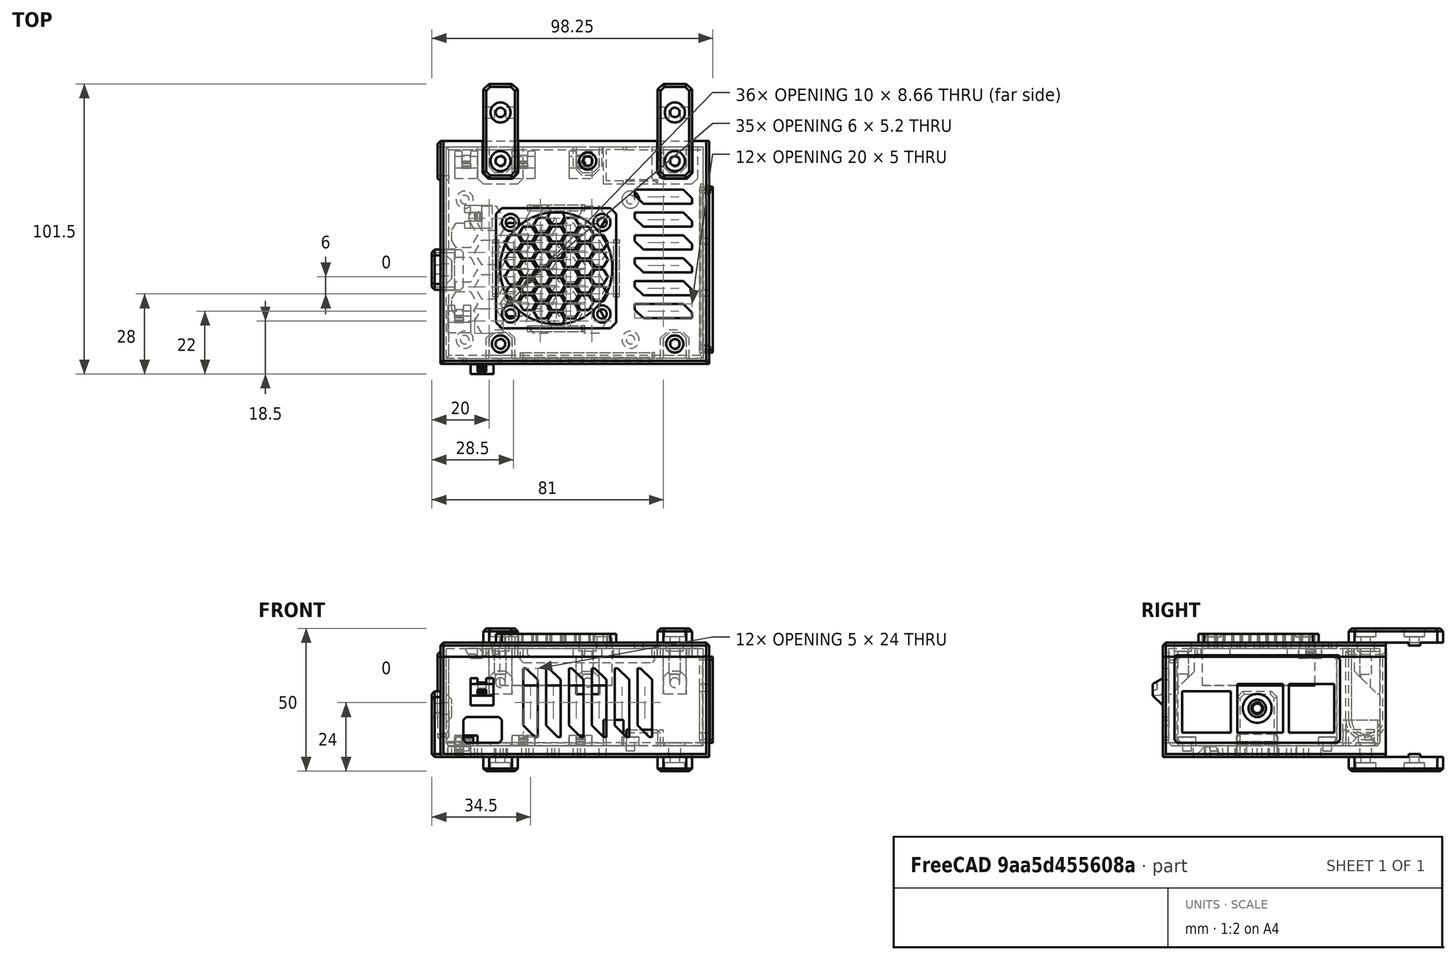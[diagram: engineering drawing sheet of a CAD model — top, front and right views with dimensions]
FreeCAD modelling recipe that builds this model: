
FCSTD DOCUMENT  (FreeCAD 0.18R16146 (Git))
Label: pi-mounter
License: All rights reserved
LicenseURL: http://en.wikipedia.org/wiki/All_rights_reserved
objects: Part::Cylinder×54, Part::MultiFuse×53, Part::Feature×52, Part::Box×50, Part::Chamfer×30, Part::Cut×28, Mesh::Feature×2
note: 267 computed .brp shape members not serialized (recipe doc carries the construction recipe); baked Part::Feature solids carry a one-line shape summary decoded from their .brp

FEATURE [Mesh::Feature] pi_pref  label="pi-pref001"
  Placement = pos=(3.5,-6,7.5) rot=(0,0,1;0rad)
FEATURE [Part::Feature] Cut003002006013012002001001_solid  label="io-panel"
  shape: bbox 4.5 x 58 x 30 mm, 38 faces (baked)
FEATURE [Part::Feature] Common001_solid  label="Common001 (Solid)"
  shape: bbox 92 x 61 x 35 mm, 183 faces (baked)
FEATURE [Part::Feature] Cut003002006013012006010  label="case-bolt012"
  Placement = pos=(19,60,25) rot=(0,0,-1;1.5708rad)
  shape: bbox 8 x 9 x 13 mm, 12 faces (baked)
FEATURE [Part::Feature] Part__Feature003  label="zip-tie-slot002"
  Placement = pos=(22.5,54,4) rot=(0,0,1;0rad)
  shape: bbox 8 x 9.5 x 3.5 mm, 30 faces (baked)
FEATURE [Part::Feature] Part__Feature005  label="zip-tie-slot004"
  Placement = pos=(2.5,54,4) rot=(0,0,1;0rad)
  shape: bbox 8 x 9.5 x 3.5 mm, 30 faces (baked)
FEATURE [Part::Cylinder] Cylinder
  Angle = 360
  AttacherType = Attacher::AttachEngine3D
  Height = 3.2
  Placement = pos=(6.5,-2.5,0) rot=(0,0,1;0rad)
  Radius = 4
FEATURE [Part::Cylinder] Cylinder001
  Angle = 360
  AttacherType = Attacher::AttachEngine3D
  Height = 3.2
  Placement = pos=(6.5,46.5,0) rot=(0,0,1;0rad)
  Radius = 4
FEATURE [Part::Cylinder] Cylinder002
  Angle = 360
  AttacherType = Attacher::AttachEngine3D
  Height = 3.2
  Placement = pos=(64.5,46.5,0) rot=(0,0,1;0rad)
  Radius = 4
FEATURE [Part::Cylinder] Cylinder003
  Angle = 360
  AttacherType = Attacher::AttachEngine3D
  Height = 3.2
  Placement = pos=(64.5,-2.5,0) rot=(0,0,1;0rad)
  Radius = 4
FEATURE [Part::Cylinder] Cylinder004
  Angle = 360
  AttacherType = Attacher::AttachEngine3D
  Height = 4
  Placement = pos=(60,20.75,0) rot=(0,0,1;0rad)
  Radius = 4
FEATURE [Part::MultiFuse] Fusion
  Shapes = -> [Cylinder004,Common001_solid]
FEATURE [Part::Cylinder] Cylinder005
  Angle = 360
  AttacherType = Attacher::AttachEngine3D
  Height = 7.5
  Placement = pos=(64.5,-2.5,0) rot=(0,0,1;0rad)
  Radius = 1.5
FEATURE [Part::Cylinder] Cylinder006
  Angle = 360
  AttacherType = Attacher::AttachEngine3D
  Height = 7.5
  Placement = pos=(64.5,46.5,0) rot=(0,0,1;0rad)
  Radius = 1.5
FEATURE [Part::Cylinder] Cylinder007
  Angle = 360
  AttacherType = Attacher::AttachEngine3D
  Height = 7.5
  Placement = pos=(6.5,-2.5,0) rot=(0,0,1;0rad)
  Radius = 1.5
FEATURE [Part::Cylinder] Cylinder008
  Angle = 360
  AttacherType = Attacher::AttachEngine3D
  Height = 7.5
  Placement = pos=(6.5,46.5,0) rot=(0,0,1;0rad)
  Radius = 1.5
FEATURE [Part::MultiFuse] Fusion001
  Shapes = -> [Cylinder003,Cylinder002,Cylinder,Cylinder001]
FEATURE [Part::MultiFuse] Fusion002
  Shapes = -> [Fusion,Fusion001]
FEATURE [Part::Cylinder] Cylinder009
  Angle = 360
  AttacherType = Attacher::AttachEngine3D
  Height = 2
  Placement = pos=(64.5,-2.5,0) rot=(0,0,1;0rad)
  Radius = 2
FEATURE [Part::Cylinder] Cylinder010
  Angle = 360
  AttacherType = Attacher::AttachEngine3D
  Height = 2
  Placement = pos=(64.5,46.5,0) rot=(0,0,1;0rad)
  Radius = 2
FEATURE [Part::Cylinder] Cylinder011
  Angle = 360
  AttacherType = Attacher::AttachEngine3D
  Height = 2
  Placement = pos=(6.5,-2.5,0) rot=(0,0,1;0rad)
  Radius = 2
FEATURE [Part::Cylinder] Cylinder012
  Angle = 360
  AttacherType = Attacher::AttachEngine3D
  Height = 2
  Placement = pos=(6.5,46.5,0) rot=(0,0,1;0rad)
  Radius = 2
FEATURE [Part::MultiFuse] Fusion003
  Shapes = -> [Cylinder005,Cylinder006,Cylinder007,Cylinder008]
FEATURE [Part::Cut] Cut
  Base = -> Fusion002
  Tool = -> Fusion003
FEATURE [Part::MultiFuse] Fusion004
  Shapes = -> [Cylinder012,Cylinder009,Cylinder010,Cylinder011]
FEATURE [Part::MultiFuse] Fusion005
  Shapes = -> [Cut,Fusion004]
FEATURE [Part::Box] Box  label="Cube"
  AttacherType = Attacher::AttachEngine3D
  Height = 10
  Length = 2
  Placement = pos=(18,-2,5.5) rot=(0,0,1;0rad)
  Width = 3
FEATURE [Part::Box] Box001  label="Cube001"
  AttacherType = Attacher::AttachEngine3D
  Height = 10
  Length = 21
  Placement = pos=(-1,-1,0) rot=(0,0,1;0rad)
  Width = 13
FEATURE [Part::Box] Box002  label="Cube002"
  AttacherType = Attacher::AttachEngine3D
  Height = 10
  Length = 19
  Placement = pos=(0,0,1) rot=(0,0,1;0rad)
  Width = 11
FEATURE [Part::Cut] Cut003002006013012006011
  Base = -> Box001
  Tool = -> Box002
FEATURE [Part::Box] Box003  label="Cube003"
  AttacherType = Attacher::AttachEngine3D
  Height = 10
  Length = 1
  Placement = pos=(6,-2,1) rot=(0,0,1;0rad)
  Width = 15
FEATURE [Part::Box] Box004  label="Cube004"
  AttacherType = Attacher::AttachEngine3D
  Height = 10
  Length = 2
  Placement = pos=(18,10,5.5) rot=(0,0,1;0rad)
  Width = 3
FEATURE [Part::MultiFuse] Fusion006
  Placement = pos=(0,0,-4.5) rot=(0,0,1;0rad)
  Shapes = -> [Box004,Box]
FEATURE [Part::Cut] Cut003002006013012006012
  Base = -> Cut003002006013012006011
  Tool = -> Box003
FEATURE [Part::Cut] Cut003002006013012006013
  Base = -> Cut003002006013012006012
  Tool = -> Fusion006
FEATURE [Part::Cylinder] Cylinder013
  Angle = 360
  AttacherType = Attacher::AttachEngine3D
  Height = 11
  Placement = pos=(7,0,6) rot=(0,1,0;1.5708rad)
  Radius = 0.5
FEATURE [Part::Cylinder] Cylinder014
  Angle = 360
  AttacherType = Attacher::AttachEngine3D
  Height = 11
  Placement = pos=(7,11,6) rot=(0,1,0;1.5708rad)
  Radius = 0.5
FEATURE [Part::Cylinder] Cylinder015
  Angle = 360
  AttacherType = Attacher::AttachEngine3D
  Height = 9
  Placement = pos=(19,10,6) rot=(0.57735,0.57735,-0.57735;2.0944rad)
  Radius = 0.5
FEATURE [Part::MultiFuse] Fusion007
  Shapes = -> [Cylinder015,Cylinder014,Cylinder013,Cut003002006013012006013]
FEATURE [Part::Box] Box005  label="Cube005"
  AttacherType = Attacher::AttachEngine3D
  Height = 10
  Length = 15
  Placement = pos=(7,-2,6.5) rot=(0,0,1;0rad)
  Width = 15
FEATURE [Part::Cut] Cut003002006013012006014  label="dcdc-mounter"
  Base = -> Fusion007
  Placement = pos=(56,53,3) rot=(0,0,1;0rad)
  Tool = -> Box005
FEATURE [Part::Feature] Part__Feature006  label="zip-tie-slot005"
  Placement = pos=(42.5,54,4) rot=(0,0,1;0rad)
  shape: bbox 8 x 9.5 x 3.5 mm, 30 faces (baked)
FEATURE [Part::Box] Box006  label="Cube006"
  AttacherType = Attacher::AttachEngine3D
  Height = 4
  Length = 92
  Placement = pos=(0,52,0) rot=(0,0,1;0rad)
  Width = 13
FEATURE [Part::Box] Box007  label="Cube007"
  AttacherType = Attacher::AttachEngine3D
  Height = 35
  Length = 92
  Placement = pos=(0,-11,0) rot=(0,0,1;0rad)
  Width = 2
FEATURE [Part::Box] Box008  label="Cube008"
  AttacherType = Attacher::AttachEngine3D
  Height = 35
  Length = 92
  Placement = pos=(0,65,0) rot=(0,0,1;0rad)
  Width = 2
FEATURE [Part::Box] Box009  label="Cube009"
  AttacherType = Attacher::AttachEngine3D
  Height = 35
  Length = 2
  Placement = pos=(90,52,0) rot=(0,0,1;0rad)
  Width = 13
FEATURE [Part::Box] Box010  label="Cube010"
  AttacherType = Attacher::AttachEngine3D
  Height = 35
  Length = 2
  Placement = pos=(-2,-11,0) rot=(0,0,1;0rad)
  Width = 78
FEATURE [Part::Box] Box011  label="Cube011"
  AttacherType = Attacher::AttachEngine3D
  Height = 4
  Length = 92
  Placement = pos=(0,-11,0) rot=(0,0,1;0rad)
  Width = 4
FEATURE [Part::Box] Box012  label="Cube012"
  AttacherType = Attacher::AttachEngine3D
  Height = 4
  Length = 4
  Placement = pos=(-2,-11,0) rot=(0,0,1;0rad)
  Width = 78
FEATURE [Part::MultiFuse] Fusion008
  Shapes = -> [Box012,Box010]
FEATURE [Part::MultiFuse] Fusion009
  Shapes = -> [Box006,Box008]
FEATURE [Part::MultiFuse] Fusion010
  Shapes = -> [Box011,Box007]
FEATURE [Part::Chamfer] Chamfer
  Base = -> Fusion008
  Edges = 1 edges r=1: [Edge28]
FEATURE [Part::Chamfer] Chamfer001
  Base = -> Fusion009
  Edges = 1 edges r=1: [Edge8]
FEATURE [Part::Chamfer] Chamfer002
  Base = -> Fusion010
  Edges = 1 edges r=1: [Edge23]
FEATURE [Part::MultiFuse] Fusion011
  Shapes = -> [Chamfer002,Chamfer001,Chamfer,Fusion005]
FEATURE [Part::MultiFuse] Fusion012
  Shapes = -> [Fusion011,Part__Feature006,Part__Feature003,Part__Feature005]
FEATURE [Part::Cylinder] Cylinder016
  Angle = 360
  AttacherType = Attacher::AttachEngine3D
  Height = 5
  Placement = pos=(19,60,0) rot=(0,0,1;0rad)
  Radius = 3.5
FEATURE [Part::Feature] Cut003002006013012006015  label="case-bolt013"
  Placement = pos=(80,60,25) rot=(0,0,-1;1.5708rad)
  shape: bbox 8 x 9 x 13 mm, 12 faces (baked)
FEATURE [Part::Feature] Cut003002006013012006016  label="case-bolt014"
  Placement = pos=(49.5,60,25) rot=(0,0,-1;1.5708rad)
  shape: bbox 8 x 9 x 13 mm, 12 faces (baked)
FEATURE [Part::Cylinder] Cylinder017
  Angle = 360
  AttacherType = Attacher::AttachEngine3D
  Height = 5
  Placement = pos=(80,60,0) rot=(0,0,1;0rad)
  Radius = 3.5
FEATURE [Part::Cylinder] Cylinder018
  Angle = 360
  AttacherType = Attacher::AttachEngine3D
  Height = 5
  Placement = pos=(80,60,0) rot=(0,0,1;0rad)
  Radius = 2.05
FEATURE [Part::Cylinder] Cylinder019
  Angle = 360
  AttacherType = Attacher::AttachEngine3D
  Height = 5
  Placement = pos=(19,60,0) rot=(0,0,1;0rad)
  Radius = 2.05
FEATURE [Part::MultiFuse] Fusion013
  Shapes = -> [Cylinder017,Cylinder016]
FEATURE [Part::MultiFuse] Fusion014
  Shapes = -> [Cylinder019,Cylinder018]
FEATURE [Part::MultiFuse] Fusion015
  Shapes = -> [Fusion012,Fusion013]
FEATURE [Part::Cut] Cut003002006013012006017
  Base = -> Fusion015
  Tool = -> Fusion014
FEATURE [Part::Feature] Cut003002006013012006018  label="case-bolt015"
  Placement = pos=(19,-4,25) rot=(0,0,1;1.5708rad)
  shape: bbox 8 x 9 x 13 mm, 12 faces (baked)
FEATURE [Part::Feature] Cut003002006013012006019  label="case-bolt016"
  Placement = pos=(80,-4,25) rot=(0,0,1;1.5708rad)
  shape: bbox 8 x 9 x 13 mm, 12 faces (baked)
FEATURE [Part::MultiFuse] Fusion016
  Shapes = -> [Cut003002006013012006019,Cut003002006013012006018,Cut003002006013012006017,Cut003002006013012006016,Cut003002006013012006015,Box009,Cut003002006013012006014,Cut003002006013012006010]
FEATURE [Part::Cylinder] Cylinder020
  Angle = 360
  AttacherType = Attacher::AttachEngine3D
  Height = 10
  Placement = pos=(-7,60,13) rot=(0,1,0;1.5708rad)
  Radius = 5
FEATURE [Part::Cylinder] Cylinder021
  Angle = 360
  AttacherType = Attacher::AttachEngine3D
  Height = 4
  Placement = pos=(-3,60,13) rot=(0,1,0;1.5708rad)
  Radius = 7
FEATURE [Part::Chamfer] Chamfer003
  Base = -> Cylinder021
  Edges = 2 edges r=1: [Edge1,Edge3]
FEATURE [Part::MultiFuse] Fusion017
  Shapes = -> [Fusion016,Chamfer003]
FEATURE [Part::Box] Box013  label="Cube013"
  AttacherType = Attacher::AttachEngine3D
  Height = 22
  Length = 10
  Placement = pos=(-7,55,13) rot=(0,0,1;0rad)
  Width = 10
FEATURE [Part::Box] Box014  label="Cube014"
  AttacherType = Attacher::AttachEngine3D
  Height = 22
  Length = 4
  Placement = pos=(-3,53,13) rot=(0,0,1;0rad)
  Width = 14
FEATURE [Part::Chamfer] Chamfer004
  Base = -> Box014
  Edges = 3 edges r=1: [Edge1,Edge3,Edge5]
FEATURE [Part::MultiFuse] Fusion018
  Shapes = -> [Box013,Cylinder020]
FEATURE [Part::MultiFuse] Fusion019
  Shapes = -> [Fusion017,Chamfer004]
FEATURE [Part::Cut] Cut003002006013012006020
  Base = -> Fusion019
  Tool = -> Fusion018
FEATURE [Part::Box] Box015  label="Cube015"
  AttacherType = Attacher::AttachEngine3D
  Height = 10
  Length = 11
  Placement = pos=(63,54,4) rot=(0,0,1;0rad)
  Width = 10
FEATURE [Part::Cut] Cut003002006013012006021
  Base = -> Cut003002006013012006020
  Tool = -> Box015
FEATURE [Part::Box] Box016  label="Cube016"
  AttacherType = Attacher::AttachEngine3D
  Height = 7
  Length = 13.5
  Placement = pos=(6,-17,7) rot=(0,0,1;0rad)
  Width = 10
FEATURE [Part::Cut] Cut003002006013012006022
  Base = -> Cut003002006013012006021
  Tool = -> Box016
FEATURE [Part::Chamfer] Chamfer005
  Base = -> Cut003002006013012006022
  Edges = 4 edges r=1: [Edge806,Edge807,Edge809,Edge811]
FEATURE [Part::Box] Box017  label="Cube017"
  AttacherType = Attacher::AttachEngine3D
  Height = 24
  Length = 5
  Placement = pos=(26,-16,7) rot=(0,0,1;0rad)
  Width = 10
FEATURE [Part::Chamfer] Chamfer006
  Base = -> Box017
  Edges = 2 edges r=4: [Edge4,Edge6]
FEATURE [Part::Feature] Chamfer006001  label="Chamfer007"
  Placement = pos=(8,0,0) rot=(0,0,1;0rad)
  shape: bbox 5 x 10 x 24 mm, 8 faces (baked)
FEATURE [Part::Feature] Chamfer006002  label="Chamfer008"
  Placement = pos=(16,0,0) rot=(0,0,1;0rad)
  shape: bbox 5 x 10 x 24 mm, 8 faces (baked)
FEATURE [Part::Feature] Chamfer006003  label="Chamfer009"
  Placement = pos=(24,0,0) rot=(0,0,1;0rad)
  shape: bbox 5 x 10 x 24 mm, 8 faces (baked)
FEATURE [Part::Feature] Chamfer006004  label="Chamfer010"
  Placement = pos=(32,0,0) rot=(0,0,1;0rad)
  shape: bbox 5 x 10 x 24 mm, 8 faces (baked)
FEATURE [Part::Feature] Chamfer006005  label="Chamfer011"
  Placement = pos=(40,0,0) rot=(0,0,1;0rad)
  shape: bbox 5 x 10 x 24 mm, 8 faces (baked)
FEATURE [Part::MultiFuse] Fusion020
  Placement = pos=(1,0,0) rot=(0,0,1;0rad)
  Shapes = -> [Chamfer006005,Chamfer006004,Chamfer006003,Chamfer006002,Chamfer006001,Chamfer006]
FEATURE [Part::Cut] Cut003002006013012006023
  Base = -> Chamfer005
  Tool = -> Fusion020
FEATURE [Part::Box] Box018  label="Cube018"
  AttacherType = Attacher::AttachEngine3D
  Height = 8.2
  Length = 7.2
  Placement = pos=(-4,14.8,0) rot=(0,0,1;0rad)
  Width = 14.4
FEATURE [Part::Chamfer] Chamfer006006
  Base = -> Box018
  Edges = 2 edges r=1: [Edge10,Edge12]
FEATURE [Part::Cylinder] Cylinder022
  Angle = 360
  AttacherType = Attacher::AttachEngine3D
  Height = 10
  Placement = pos=(-6,22,17) rot=(0,1,0;1.5708rad)
  Radius = 2.05
FEATURE [Part::Cylinder] Cylinder023
  Angle = 360
  AttacherType = Attacher::AttachEngine3D
  Height = 4
  Placement = pos=(-2,22,17) rot=(0,1,0;1.5708rad)
  Radius = 5.05
FEATURE [Part::Chamfer] Chamfer006007
  Base = -> Cylinder023
  Edges = 1 edges r=2: [Edge1]
FEATURE [Part::Cut] Cut003002006013012006024
  Base = -> Cut003002006013012006023
  Tool = -> Chamfer006006
FEATURE [Part::MultiFuse] Fusion021
  Shapes = -> [Cut003002006013012006024,Chamfer006007]
FEATURE [Part::Cut] Cut003002006013012006025  label="case-r1"
  Base = -> Fusion021
  Tool = -> Cylinder022
FEATURE [Part::Cylinder] Cylinder024
  Angle = 360
  AttacherType = Attacher::AttachEngine3D
  Height = 10
  Placement = pos=(19,60,-5) rot=(0,0,1;0rad)
  Radius = 1.65
FEATURE [Part::Box] Box019  label="Cube019"
  AttacherType = Attacher::AttachEngine3D
  Height = 5
  Length = 12
  Placement = pos=(13,54,40) rot=(0,0,1;0rad)
  Width = 33
FEATURE [Part::Cylinder] Cylinder026
  Angle = 360
  AttacherType = Attacher::AttachEngine3D
  Height = 10
  Placement = pos=(19,77,-5) rot=(0,0,1;0rad)
  Radius = 1.65
FEATURE [Part::Box] Box020  label="Cube020"
  AttacherType = Attacher::AttachEngine3D
  Height = 5
  Length = 12
  Placement = pos=(13,54,-5) rot=(0,0,1;0rad)
  Width = 33
FEATURE [Part::Cylinder] Cylinder027
  Angle = 360
  AttacherType = Attacher::AttachEngine3D
  Height = 3
  Placement = pos=(19,77,-5) rot=(0,0,1;0rad)
  Radius = 3.5
FEATURE [Part::Cylinder] Cylinder028
  Angle = 360
  AttacherType = Attacher::AttachEngine3D
  Height = 3
  Placement = pos=(19,60,-5) rot=(0,0,1;0rad)
  Radius = 3.5
FEATURE [Part::MultiFuse] Fusion022
  Shapes = -> [Cylinder026,Cylinder024]
FEATURE [Part::Cut] Cut003002006013012006025002
  Base = -> Box020
  Tool = -> Fusion022
FEATURE [Part::MultiFuse] Fusion023
  Shapes = -> [Cylinder028,Cylinder027]
FEATURE [Part::Cut] Cut003002006013012006025003
  Base = -> Cut003002006013012006025002
  Tool = -> Fusion023
FEATURE [Part::Chamfer] Chamfer006009
  Base = -> Cut003002006013012006025003
  Edges = 4 edges r=2: [Edge1,Edge3,Edge6,Edge13]
FEATURE [Part::Chamfer] Chamfer006010
  Base = -> Chamfer006009
  Edges = 8 edges r=1: [Edge4,Edge14,Edge16,Edge18,Edge19,Edge20,Edge21,Edge22]
FEATURE [Part::Box] Box021  label="Cube021"
  AttacherType = Attacher::AttachEngine3D
  Height = 1
  Length = 4
  Placement = pos=(13,75,0) rot=(0,0,1;0rad)
  Width = 4
FEATURE [Part::Box] Box022  label="Cube022"
  AttacherType = Attacher::AttachEngine3D
  Height = 1
  Length = 4
  Placement = pos=(21,75,0) rot=(0,0,1;0rad)
  Width = 4
FEATURE [Part::MultiFuse] Fusion024  label="mounter-small"
  Shapes = -> [Box022,Box021,Chamfer006010]
FEATURE [Part::Feature] Fusion024001  label="mounter-small001"
  Placement = pos=(61,0,0) rot=(0,0,1;0rad)
  shape: bbox 12 x 33 x 6 mm, 34 faces (baked)
FEATURE [Part::Box] Box023  label="Cube023"
  AttacherType = Attacher::AttachEngine3D
  Height = 5
  Length = 12
  Placement = pos=(13,54,35) rot=(0,0,1;0rad)
  Width = 13
FEATURE [Part::Box] Box024  label="Cube024"
  AttacherType = Attacher::AttachEngine3D
  Height = 5
  Length = 12.4
  Placement = pos=(12.8,53.8,35) rot=(0,0,1;0rad)
  Width = 13.2
FEATURE [Part::MultiFuse] Fusion024002
  Shapes = -> [Box019,Box023]
FEATURE [Part::Chamfer] Chamfer006011
  Base = -> Fusion024002
  Edges = 4 edges r=2: [Edge1,Edge3,Edge7,Edge12]
FEATURE [Part::Chamfer] Chamfer006012
  Base = -> Chamfer006011
  Edges = 8 edges r=1: [Edge1,Edge6,Edge7,Edge8,Edge9,Edge10,Edge11,Edge12]
FEATURE [Part::Cylinder] Cylinder029
  Angle = 360
  AttacherType = Attacher::AttachEngine3D
  Height = 3
  Placement = pos=(19,77,32) rot=(0,0,1;0rad)
  Radius = 3.5
FEATURE [Part::Cylinder] Cylinder030
  Angle = 360
  AttacherType = Attacher::AttachEngine3D
  Height = 3
  Placement = pos=(19,60,32) rot=(0,0,1;0rad)
  Radius = 3.5
FEATURE [Part::Cylinder] Cylinder031
  Angle = 360
  AttacherType = Attacher::AttachEngine3D
  Height = 15
  Placement = pos=(19,60,32) rot=(0,0,1;0rad)
  Radius = 1.65
FEATURE [Part::Cylinder] Cylinder032
  Angle = 360
  AttacherType = Attacher::AttachEngine3D
  Height = 15
  Placement = pos=(19,77,32) rot=(0,0,1;0rad)
  Radius = 1.65
FEATURE [Part::MultiFuse] Fusion024003
  Shapes = -> [Cylinder032,Cylinder031]
FEATURE [Part::Cut] Cut003002006013012006025004
  Base = -> Chamfer006012
  Tool = -> Fusion024003
FEATURE [Part::MultiFuse] Fusion024004
  Placement = pos=(0,0,10) rot=(0,0,1;0rad)
  Shapes = -> [Cylinder030,Cylinder029]
FEATURE [Part::Cut] Cut003002006013012006025005
  Base = -> Cut003002006013012006025004
  Tool = -> Fusion024004
FEATURE [Part::Box] Box025  label="Cube025"
  AttacherType = Attacher::AttachEngine3D
  Height = 1
  Length = 4
  Placement = pos=(13,75,0) rot=(0,0,1;0rad)
  Width = 4
FEATURE [Part::Box] Box026  label="Cube026"
  AttacherType = Attacher::AttachEngine3D
  Height = 1
  Length = 4
  Placement = pos=(21,75,0) rot=(0,0,1;0rad)
  Width = 4
FEATURE [Part::MultiFuse] Fusion024005
  Placement = pos=(0,0,39) rot=(0,0,1;0rad)
  Shapes = -> [Box026,Box025]
FEATURE [Part::MultiFuse] Fusion024006  label="mounter-big"
  Shapes = -> [Fusion024005,Cut003002006013012006025005]
FEATURE [Part::Feature] Fusion024006001  label="mounter-big001"
  Placement = pos=(61,0,0) rot=(0,0,1;0rad)
  shape: bbox 12 x 33 x 10 mm, 34 faces (baked)
FEATURE [Part::Chamfer] Chamfer006013  label="door-cutout"
  Base = -> Box024
  Edges = 2 edges r=2: [Edge1,Edge5]
FEATURE [Part::Feature] Chamfer006013001  label="door-cutout001"
  Placement = pos=(61,0,0) rot=(0,0,1;0rad)
  shape: bbox 12.4 x 13.2 x 5 mm, 8 faces (baked)
FEATURE [Part::Box] Box027  label="Cube027"
  AttacherType = Attacher::AttachEngine3D
  Height = 5
  Length = 94
  Placement = pos=(-2,-11,35) rot=(0,0,1;0rad)
  Width = 78
FEATURE [Part::Box] Box028  label="Cube028"
  AttacherType = Attacher::AttachEngine3D
  Height = 3
  Length = 90
  Placement = pos=(0,-9,35) rot=(0,0,1;0rad)
  Width = 74
FEATURE [Part::Box] Box029  label="Cube029"
  AttacherType = Attacher::AttachEngine3D
  Height = 3
  Length = 16
  Placement = pos=(11,52,35) rot=(0,0,1;0rad)
  Width = 15
FEATURE [Part::Box] Box031  label="Cube031"
  AttacherType = Attacher::AttachEngine3D
  Height = 3
  Length = 16
  Placement = pos=(72,52,35) rot=(0,0,1;0rad)
  Width = 15
FEATURE [Part::Cut] Cut003002006013012006025006
  Base = -> Box027
  Tool = -> Box028
FEATURE [Part::Chamfer] Chamfer006013002
  Base = -> Box031
  Edges = 2 edges r=2: [Edge1,Edge5]
FEATURE [Part::Chamfer] Chamfer006013003
  Base = -> Box029
  Edges = 2 edges r=2: [Edge1,Edge5]
FEATURE [Part::MultiFuse] Fusion024006002
  Shapes = -> [Chamfer006013003,Chamfer006013002,Cut003002006013012006025006]
FEATURE [Part::MultiFuse] Fusion024006003
  Shapes = -> [Chamfer006013,Chamfer006013001]
FEATURE [Part::Cut] Cut003002006013012006025007
  Base = -> Fusion024006002
  Tool = -> Fusion024006003
FEATURE [Part::Cylinder] Cylinder033
  Angle = 360
  AttacherType = Attacher::AttachEngine3D
  Height = 10
  Placement = pos=(19,-4,26) rot=(0,0,1;0rad)
  Radius = 1.65
FEATURE [Part::Cylinder] Cylinder034
  Angle = 360
  AttacherType = Attacher::AttachEngine3D
  Height = 10
  Placement = pos=(80,-4,26) rot=(0,0,1;0rad)
  Radius = 1.65
FEATURE [Part::Cylinder] Cylinder035
  Angle = 360
  AttacherType = Attacher::AttachEngine3D
  Height = 10
  Placement = pos=(49.5,60,26) rot=(0,0,1;0rad)
  Radius = 1.65
FEATURE [Part::Cylinder] Cylinder036
  Angle = 360
  AttacherType = Attacher::AttachEngine3D
  Height = 3
  Placement = pos=(49.5,60,26) rot=(0,0,1;0rad)
  Radius = 3
FEATURE [Part::Cylinder] Cylinder037
  Angle = 360
  AttacherType = Attacher::AttachEngine3D
  Height = 3
  Placement = pos=(80,-4,26) rot=(0,0,1;0rad)
  Radius = 3
FEATURE [Part::Cylinder] Cylinder038
  Angle = 360
  AttacherType = Attacher::AttachEngine3D
  Height = 3
  Placement = pos=(19,-4,26) rot=(0,0,1;0rad)
  Radius = 3
FEATURE [Part::MultiFuse] Fusion024006004
  Placement = pos=(0,0,11) rot=(0,0,1;0rad)
  Shapes = -> [Cylinder036,Cylinder037,Cylinder038]
FEATURE [Part::MultiFuse] Fusion024006005
  Placement = pos=(0,0,5.5) rot=(0,0,1;0rad)
  Shapes = -> [Cylinder035,Cylinder034,Cylinder033]
FEATURE [Part::MultiFuse] Fusion024006006
  Shapes = -> [Fusion024006005,Fusion024006004]
FEATURE [Part::Box] Box032  label="Cube032"
  AttacherType = Attacher::AttachEngine3D
  Height = 5
  Length = 10
  Placement = pos=(14,-9,36) rot=(0,0,1;0rad)
  Width = 10
FEATURE [Part::Box] Box033  label="Cube033"
  AttacherType = Attacher::AttachEngine3D
  Height = 5
  Length = 10
  Placement = pos=(75,-9,36) rot=(0,0,1;0rad)
  Width = 10
FEATURE [Part::Box] Box034  label="Cube034"
  AttacherType = Attacher::AttachEngine3D
  Height = 5
  Length = 10
  Placement = pos=(44.5,55,36) rot=(0,0,1;0rad)
  Width = 10
FEATURE [Part::MultiFuse] Fusion024006007
  Placement = pos=(0,0,-1) rot=(0,0,1;0rad)
  Shapes = -> [Box034,Box033,Box032]
FEATURE [Part::Chamfer] Chamfer006013004
  Base = -> Fusion024006007
  Edges = 6 edges r=3: [Edge1,Edge5,Edge15,Edge19,Edge27,Edge31]
FEATURE [Part::MultiFuse] Fusion024006008
  Shapes = -> [Cut003002006013012006025007,Chamfer006013004]
FEATURE [Part::Cut] Cut003002006013012006025008
  Base = -> Fusion024006008
  Tool = -> Fusion024006006
FEATURE [Part::Box] Box035  label="Cube035"
  AttacherType = Attacher::AttachEngine3D
  Height = 10
  Length = 14
  Placement = pos=(86.5,-7,25.5) rot=(0,0,1;0rad)
  Width = 58
FEATURE [Part::Chamfer] Chamfer006013005
  Base = -> Box035
  Edges = 2 edges r=0.5: [Edge10,Edge12]
FEATURE [Part::Cut] Cut003002006013012006025009
  Base = -> Cut003002006013012006025008
  Tool = -> Chamfer006013005
FEATURE [Part::Box] Box036  label="Cube036"
  AttacherType = Attacher::AttachEngine3D
  Height = 2
  Length = 2
  Placement = pos=(-3,53,35) rot=(0,0,1;0rad)
  Width = 14
FEATURE [Part::Chamfer] Chamfer006013006
  Base = -> Box036
  Edges = 3 edges r=1: [Edge1,Edge2,Edge3]
FEATURE [Part::MultiFuse] Fusion024006009
  Shapes = -> [Cut003002006013012006025009,Chamfer006013006]
FEATURE [Part::Chamfer] Chamfer006013007
  Base = -> Fusion024006009
  Edges = 5 edges r=1: [Edge170,Edge172,Edge173,Edge174,Edge175]
FEATURE [Mesh::Feature] fan4010_v2
  Placement = pos=(18.5,2.5,22) rot=(0,0,1;0rad)
FEATURE [Part::Cylinder] Cylinder039
  Angle = 360
  AttacherType = Attacher::AttachEngine3D
  Height = 10
  Placement = pos=(22.5,6.5,0) rot=(0,0,1;0rad)
  Radius = 1.65
FEATURE [Part::Cylinder] Cylinder040
  Angle = 360
  AttacherType = Attacher::AttachEngine3D
  Height = 10
  Placement = pos=(54.5,6.5,0) rot=(0,0,1;0rad)
  Radius = 1.65
FEATURE [Part::Cylinder] Cylinder041
  Angle = 360
  AttacherType = Attacher::AttachEngine3D
  Height = 10
  Placement = pos=(54.5,38.5,0) rot=(0,0,1;0rad)
  Radius = 1.65
FEATURE [Part::Cylinder] Cylinder042
  Angle = 360
  AttacherType = Attacher::AttachEngine3D
  Height = 10
  Placement = pos=(22.5,38.5,0) rot=(0,0,1;0rad)
  Radius = 1.65
FEATURE [Part::Cylinder] Cylinder043
  Angle = 360
  AttacherType = Attacher::AttachEngine3D
  Height = 18
  Placement = pos=(38.5,22.5,25) rot=(0,0,1;0rad)
  Radius = 19.65
FEATURE [Part::Box] Box037  label="Cube037"
  AttacherType = Attacher::AttachEngine3D
  Height = 3
  Length = 42
  Placement = pos=(17.5,1.5,0) rot=(0,0,1;0rad)
  Width = 42
FEATURE [Part::Cylinder] Cylinder044
  Angle = 360
  AttacherType = Attacher::AttachEngine3D
  Height = 10
  Placement = pos=(22.5,6.5,0) rot=(0,0,1;0rad)
  Radius = 1.65
FEATURE [Part::Cylinder] Cylinder045
  Angle = 360
  AttacherType = Attacher::AttachEngine3D
  Height = 10
  Placement = pos=(54.5,38.5,0) rot=(0,0,1;0rad)
  Radius = 1.65
FEATURE [Part::Cylinder] Cylinder046
  Angle = 360
  AttacherType = Attacher::AttachEngine3D
  Height = 10
  Placement = pos=(54.5,6.5,0) rot=(0,0,1;0rad)
  Radius = 1.65
FEATURE [Part::Cylinder] Cylinder047
  Angle = 360
  AttacherType = Attacher::AttachEngine3D
  Height = 10
  Placement = pos=(22.5,38.5,0) rot=(0,0,1;0rad)
  Radius = 1.65
FEATURE [Part::Cylinder] Cylinder048
  Angle = 360
  AttacherType = Attacher::AttachEngine3D
  Height = 18
  Placement = pos=(38.5,22.5,0) rot=(0,0,1;0rad)
  Radius = 19.65
FEATURE [Part::MultiFuse] Fusion024006010
  Placement = pos=(0,0,33) rot=(0,0,1;0rad)
  Shapes = -> [Cylinder048,Cylinder047,Cylinder046,Cylinder045,Cylinder044]
FEATURE [Part::Cut] Cut003002006013012006025010
  Base = -> Chamfer006013007
  Tool = -> Fusion024006010
FEATURE [Part::Box] Box038  label="Cube038"
  AttacherType = Attacher::AttachEngine3D
  Height = 3
  Length = 20
  Placement = pos=(28.5,0.35,35) rot=(0,0,1;0rad)
  Width = 2
FEATURE [Part::Box] Box040  label="Cube040"
  AttacherType = Attacher::AttachEngine3D
  Height = 3
  Length = 20
  Placement = pos=(28.5,42.65,35) rot=(0,0,1;0rad)
  Width = 2
FEATURE [Part::Box] Box041  label="Cube041"
  AttacherType = Attacher::AttachEngine3D
  Height = 3
  Length = 2
  Placement = pos=(58.65,12.5,35) rot=(0,0,1;0rad)
  Width = 20
FEATURE [Part::Box] Box042  label="Cube042"
  AttacherType = Attacher::AttachEngine3D
  Height = 3
  Length = 2
  Placement = pos=(16.35,12.5,35) rot=(0,0,1;0rad)
  Width = 20
FEATURE [Part::MultiFuse] Fusion024006011
  Shapes = -> [Box042,Box041,Box040,Box038]
FEATURE [Part::Box] Box044  label="Cube044"
  AttacherType = Attacher::AttachEngine3D
  Height = 5
  Length = 47
  Placement = pos=(26,-8.7,33) rot=(0,0,1;0rad)
  Width = 1.7
FEATURE [Part::Chamfer] Chamfer006013008
  Base = -> Box044
  Edges = 2 edges r=1: [Edge4,Edge8]
FEATURE [Part::Chamfer] Chamfer006013009
  Base = -> Fusion024006011
  Edges = 8 edges r=1: [Edge9,Edge11,Edge21,Edge23,Edge28,Edge32,Edge40,Edge44]
FEATURE [Part::MultiFuse] Fusion024006012
  Shapes = -> [Chamfer006013008,Cut003002006013012006025010,Chamfer006013009]
FEATURE [Part::Box] Box045  label="Cube045"
  AttacherType = Attacher::AttachEngine3D
  Height = 10
  Length = 20
  Placement = pos=(66,6,34) rot=(0,0,1;0rad)
  Width = 5
FEATURE [Part::Chamfer] Chamfer006013010
  Base = -> Box045
  Edges = 2 edges r=3: [Edge1,Edge7]
FEATURE [Part::Feature] Chamfer006013010001  label="Chamfer006013011"
  Placement = pos=(0,8,0) rot=(0,0,1;0rad)
  shape: bbox 20 x 5 x 10 mm, 8 faces (baked)
FEATURE [Part::Feature] Chamfer006013010002  label="Chamfer006013012"
  Placement = pos=(0,16,0) rot=(0,0,1;0rad)
  shape: bbox 20 x 5 x 10 mm, 8 faces (baked)
FEATURE [Part::Feature] Chamfer006013010003  label="Chamfer006013013"
  Placement = pos=(0,24,0) rot=(0,0,1;0rad)
  shape: bbox 20 x 5 x 10 mm, 8 faces (baked)
FEATURE [Part::Feature] Chamfer006013010004  label="Chamfer006013014"
  Placement = pos=(0,32,0) rot=(0,0,1;0rad)
  shape: bbox 20 x 5 x 10 mm, 8 faces (baked)
FEATURE [Part::Feature] Chamfer006013010005  label="Chamfer006013015"
  Placement = pos=(0,40,0) rot=(0,0,1;0rad)
  shape: bbox 20 x 5 x 10 mm, 8 faces (baked)
FEATURE [Part::MultiFuse] Fusion024006013
  Placement = pos=(0,-1,0) rot=(0,0,1;0rad)
  Shapes = -> [Chamfer006013010005,Chamfer006013010004,Chamfer006013010003,Chamfer006013010002,Chamfer006013010001,Chamfer006013010]
FEATURE [Part::Cut] Cut003002006013012006025011
  Base = -> Fusion024006012
  Tool = -> Fusion024006013
FEATURE [Part::Feature] Part__Feature001  label="zip-tie-slot"
  shape: bbox 8 x 9.5 x 3.5 mm, 30 faces (baked)
FEATURE [Part::Feature] Part__Feature007  label="zip-tie-slot006"
  Placement = pos=(16,45,38) rot=(0.707107,-0.707107,0;3.14159rad)
  shape: bbox 9.5 x 8 x 3.5 mm, 30 faces (baked)
FEATURE [Part::Box] Box046  label="Cube046"
  AttacherType = Attacher::AttachEngine3D
  Height = 23
  Length = 3
  Placement = pos=(-5,15,0) rot=(0,0,1;0rad)
  Width = 14
FEATURE [Part::Box] Box047  label="Cube047"
  AttacherType = Attacher::AttachEngine3D
  Height = 8
  Length = 2
  Placement = pos=(-2,15,0) rot=(0,0,1;0rad)
  Width = 14
FEATURE [Part::Box] Box048  label="Cube048"
  AttacherType = Attacher::AttachEngine3D
  Height = 5.5
  Length = 3
  Placement = pos=(0,15,0) rot=(0,0,1;0rad)
  Width = 14
FEATURE [Part::Chamfer] Chamfer006013010006
  Base = -> Box047
  Edges = 2 edges r=1: [Edge10,Edge12]
FEATURE [Part::Box] Box049  label="Cube049"
  AttacherType = Attacher::AttachEngine3D
  Height = 1.2
  Length = 3
  Placement = pos=(3,15,4.3) rot=(0,0,1;0rad)
  Width = 14
FEATURE [Part::Chamfer] Chamfer006013010007
  Base = -> Box049
  Edges = 2 edges r=1: [Edge5,Edge7]
FEATURE [Part::Cylinder] Cylinder049
  Angle = 360
  AttacherType = Attacher::AttachEngine3D
  Height = 1
  Placement = pos=(-4,22,17) rot=(0,-1,0;1.5708rad)
  Radius = 3
FEATURE [Part::Cylinder] Cylinder050
  Angle = 360
  AttacherType = Attacher::AttachEngine3D
  Height = 10
  Placement = pos=(2,22,17) rot=(0,-1,0;1.5708rad)
  Radius = 1.65
FEATURE [Part::Chamfer] Chamfer006013010008
  Base = -> Box046
  Edges = 2 edges r=2: [Edge10,Edge12]
FEATURE [Part::MultiFuse] Fusion024006014002
  Shapes = -> [Chamfer006013010008,Chamfer006013010006,Box048,Chamfer006013010007]
FEATURE [Part::MultiFuse] Fusion024006014003
  Shapes = -> [Cylinder050,Cylinder049]
FEATURE [Part::Cut] Cut003002006013012006025012
  Base = -> Fusion024006014002
  Tool = -> Fusion024006014003
FEATURE [Part::Chamfer] Chamfer006013010009  label="sd-lock"
  Base = -> Cut003002006013012006025012
  Edges = 8 edges r=1: [Edge46,Edge47,Edge52,Edge53,Edge54,Edge60,Edge62,Edge63]
FEATURE [Part::MultiFuse] Fusion024006014  label="door-r1-base"
  Shapes = -> [Part__Feature007,Cut003002006013012006025011]
FEATURE [Part::Cylinder] Cylinder051
  Angle = 360
  AttacherType = Attacher::AttachEngine3D
  Height = 1
  Placement = pos=(22.5,38.5,0) rot=(0,0,1;0rad)
  Radius = 3
FEATURE [Part::Cylinder] Cylinder052
  Angle = 360
  AttacherType = Attacher::AttachEngine3D
  Height = 1
  Placement = pos=(22.5,6.5,0) rot=(0,0,1;0rad)
  Radius = 3
FEATURE [Part::Cylinder] Cylinder053
  Angle = 360
  AttacherType = Attacher::AttachEngine3D
  Height = 1
  Placement = pos=(54.5,6.5,0) rot=(0,0,1;0rad)
  Radius = 3
FEATURE [Part::Cylinder] Cylinder054
  Angle = 360
  AttacherType = Attacher::AttachEngine3D
  Height = 1
  Placement = pos=(54.5,38.5,0) rot=(0,0,1;0rad)
  Radius = 3
FEATURE [Part::MultiFuse] Fusion024006014004
  Shapes = -> [Cylinder042,Cylinder039,Cylinder040,Cylinder041]
FEATURE [Part::MultiFuse] Fusion024006014005
  Placement = pos=(0,0,2) rot=(0,0,1;0rad)
  Shapes = -> [Cylinder054,Cylinder053,Cylinder052,Cylinder051]
FEATURE [Part::MultiFuse] Fusion024006014006
  Shapes = -> [Fusion024006014005,Fusion024006014004]
FEATURE [Part::Chamfer] Chamfer006013010010
  Base = -> Box037
  Edges = 4 edges r=2: [Edge1,Edge3,Edge5,Edge7]
FEATURE [Part::Cut] Cut003002006013012006025013
  Base = -> Chamfer006013010010
  Placement = pos=(-38.5,-22.5,0) rot=(0,0,1;0rad)
  Tool = -> Fusion024006014006
FEATURE [Part::Feature] Body001
  shape: bbox 6 x 5.196 x 10 mm, 8 faces (baked)
FEATURE [Part::Feature] Body002
  Placement = pos=(5,3,0) rot=(0,0,1;0rad)
  shape: bbox 6 x 5.196 x 10 mm, 8 faces (baked)
FEATURE [Part::Feature] Body003
  Placement = pos=(10,0,0) rot=(0,0,1;0rad)
  shape: bbox 6 x 5.196 x 10 mm, 8 faces (baked)
FEATURE [Part::Feature] Body004
  Placement = pos=(15,3,0) rot=(0,0,1;0rad)
  shape: bbox 6 x 5.196 x 10 mm, 8 faces (baked)
FEATURE [Part::Feature] Body005
  Placement = pos=(-5,3,0) rot=(0,0,1;0rad)
  shape: bbox 6 x 5.196 x 10 mm, 8 faces (baked)
FEATURE [Part::Feature] Body006
  Placement = pos=(-10,0,0) rot=(0,0,1;0rad)
  shape: bbox 6 x 5.196 x 10 mm, 8 faces (baked)
FEATURE [Part::Feature] Body007
  Placement = pos=(-15,3,0) rot=(0,0,1;0rad)
  shape: bbox 6 x 5.196 x 10 mm, 8 faces (baked)
FEATURE [Part::Feature] Body008
  Placement = pos=(-15,3,0) rot=(0,0,1;0rad)
  shape: bbox 6 x 5.196 x 10 mm, 8 faces (baked)
FEATURE [Part::Feature] Body009
  Placement = pos=(-5,3,0) rot=(0,0,1;0rad)
  shape: bbox 6 x 5.196 x 10 mm, 8 faces (baked)
FEATURE [Part::Feature] Body010
  Placement = pos=(5,3,0) rot=(0,0,1;0rad)
  shape: bbox 6 x 5.196 x 10 mm, 8 faces (baked)
FEATURE [Part::Feature] Body011
  Placement = pos=(15,3,0) rot=(0,0,1;0rad)
  shape: bbox 6 x 5.196 x 10 mm, 8 faces (baked)
FEATURE [Part::MultiFuse] Fusion024006014007
  Placement = pos=(0,-6,0) rot=(0,0,1;0rad)
  Shapes = -> [Body011,Body010,Body009,Body008]
FEATURE [Part::Feature] Body012
  Placement = pos=(-10,0,0) rot=(0,0,1;0rad)
  shape: bbox 6 x 5.196 x 10 mm, 8 faces (baked)
FEATURE [Part::Feature] Body013
  shape: bbox 6 x 5.196 x 10 mm, 8 faces (baked)
FEATURE [Part::Feature] Body014
  Placement = pos=(10,0,0) rot=(0,0,1;0rad)
  shape: bbox 6 x 5.196 x 10 mm, 8 faces (baked)
FEATURE [Part::MultiFuse] Fusion024006014008
  Placement = pos=(0,-6,0) rot=(0,0,1;0rad)
  Shapes = -> [Body014,Body013,Body012]
FEATURE [Part::Feature] Fusion024006014008001  label="Fusion024006014009"
  Placement = pos=(0,6,0) rot=(0,0,1;0rad)
  shape: bbox 26 x 5.196 x 10 mm, 24 faces, 3 solids (baked)
FEATURE [Part::Feature] Fusion024006014007001  label="Fusion024006014010"
  Placement = pos=(0,6,0) rot=(0,0,1;0rad)
  shape: bbox 36 x 5.196 x 10 mm, 32 faces, 4 solids (baked)
FEATURE [Part::Feature] Fusion024006014008002  label="Fusion024006014011"
  Placement = pos=(0,-12,0) rot=(0,0,1;0rad)
  shape: bbox 26 x 5.196 x 10 mm, 24 faces, 3 solids (baked)
FEATURE [Part::Feature] Fusion024006014008003  label="Fusion024006014012"
  Placement = pos=(0,-12,0) rot=(0,0,1;0rad)
  shape: bbox 36 x 5.196 x 10 mm, 32 faces, 4 solids (baked)
FEATURE [Part::Feature] Fusion024006014008004  label="Fusion024006014013"
  Placement = pos=(0,12,0) rot=(0,0,1;0rad)
  shape: bbox 26 x 5.196 x 10 mm, 24 faces, 3 solids (baked)
FEATURE [Part::Feature] Body015
  Placement = pos=(-5,15,0) rot=(0,0,1;0rad)
  shape: bbox 6 x 5.196 x 10 mm, 8 faces (baked)
FEATURE [Part::Feature] Body016
  Placement = pos=(5,15,0) rot=(0,0,1;0rad)
  shape: bbox 6 x 5.196 x 10 mm, 8 faces (baked)
FEATURE [Part::MultiFuse] Fusion024006014008005
  Shapes = -> [Body016,Body015]
FEATURE [Part::Feature] Fusion024006014008005001  label="Fusion024006014008006"
  Placement = pos=(0,-30,0) rot=(0,0,1;0rad)
  shape: bbox 16 x 5.196 x 10 mm, 16 faces, 2 solids (baked)
FEATURE [Part::Feature] Body017
  Placement = pos=(0,18,0) rot=(0,0,1;0rad)
  shape: bbox 6 x 5.196 x 10 mm, 8 faces (baked)
FEATURE [Part::Feature] Body018
  Placement = pos=(0,-18,0) rot=(0,0,1;0rad)
  shape: bbox 6 x 5.196 x 10 mm, 8 faces (baked)
FEATURE [Part::Box] Box050  label="Cube050"
  AttacherType = Attacher::AttachEngine3D
  Height = 10
  Length = 10
  Placement = pos=(-4.5,19.5,0) rot=(0,0,1;0rad)
  Width = 10
FEATURE [Part::Box] Box051  label="Cube051"
  AttacherType = Attacher::AttachEngine3D
  Height = 10
  Length = 10
  Placement = pos=(-4.5,-29.5,0) rot=(0,0,1;0rad)
  Width = 10
FEATURE [Part::Cut] Cut003002006013012006025014
  Base = -> Body017
  Tool = -> Box050
FEATURE [Part::Cut] Cut003002006013012006025015
  Base = -> Body018
  Tool = -> Box051
FEATURE [Part::MultiFuse] Fusion024006014008005002
  Shapes = -> [Cut003002006013012006025015,Cut003002006013012006025014,Body001,Body002,Body003,Body004,Body005,Body006,Body007,Fusion024006014007,Fusion024006014008,Fusion024006014008001,Fusion024006014007001,Fusion024006014008002,Fusion024006014008003,Fusion024006014008004,Fusion024006014008005,Fusion024006014008005001]
FEATURE [Part::Cut] Cut003002006013012006025016  label="fan-fin"
  Base = -> Cut003002006013012006025013
  Placement = pos=(38.5,22.5,40) rot=(0,0,1;0rad)
  Tool = -> Fusion024006014008005002
FEATURE [Part::Feature] Fusion024006014008005003  label="door-r1-base001"
  shape: bbox 95 x 78 x 7 mm, 181 faces (baked)
FEATURE [Part::Box] Box052  label="Cube052"
  AttacherType = Attacher::AttachEngine3D
  Height = 4
  Length = 13.5
  Placement = pos=(6,-18,5) rot=(0,0,1;0rad)
  Width = 10
FEATURE [Part::Chamfer] Chamfer006013010011  label="micro-sd-extend"
  Base = -> Box052
  Edges = 2 edges r=1: [Edge4,Edge8]
FEATURE [Part::Cut] Cut003002006013012006025017
  Base = -> Cut003002006013012006025
  Tool = -> Chamfer006013010011
FEATURE [Part::Feature] Part__Feature008  label="zip-tie-slot007"
  Placement = pos=(8,-11,18) rot=(1,0,0;1.5708rad)
  shape: bbox 8 x 3.5 x 9.5 mm, 30 faces (baked)
FEATURE [Part::MultiFuse] Fusion024006014008005004  label="bas-r1-f1"
  Shapes = -> [Cut003002006013012006025017,Part__Feature008]
FEATURE [Part::Feature] Fusion024006014008005004001  label="bas-r1-f002"
  shape: bbox 95 x 81.5 x 35 mm, 429 faces (baked)
FEATURE [Part::Chamfer] Chamfer006013010012  label="base-r1-f1-chamfer"
  Base = -> Fusion024006014008005004001
  Edges = 6 edges r=1: [Edge423,Edge424,Edge426,Edge427,Edge1163,Edge1164]
